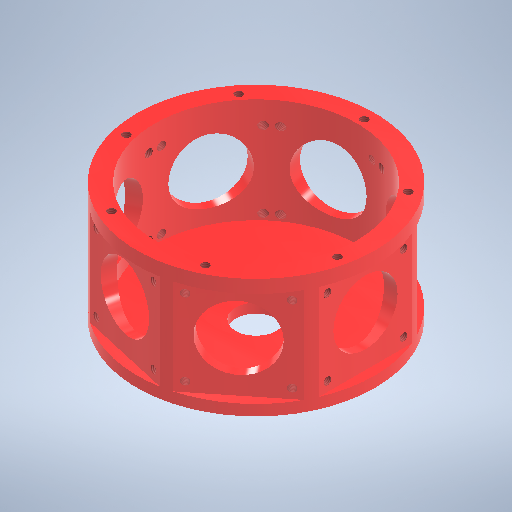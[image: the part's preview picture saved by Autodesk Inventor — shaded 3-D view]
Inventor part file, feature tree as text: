
AUTODESK INVENTOR PART (.ipt)
format: ipt  version: 2025 (Build 290162010, 162A)  size: 514,560 bytes
history: native  units: mm
features: sketch x11, extrude x6, hole x6, pattern_circular x5, plane x1
ambient origin geometry x8: Origin, YZ Plane, XZ Plane, XY Plane, X Axis, Y Axis, Z Axis, Center Point
bodies: Volumenkörper1 (feature_tree)
feature tree (29):
  extrude  "Extrusion1"  Depth=50.0mm TaperAngle=0.0deg
  plane  "Arbeitsebene1"
  extrude  "Extrusion2"  Depth=50.0mm
  pattern_circular  "Runde Anordnung1"  Count=4  [1 undecoded]
  sketch  "Skizze6"  dims[d7=4.0mm d8=0.0mm d9=70.0mm d10=360.0deg]
  extrude  "Extrusion9"  Depth=4.0mm TaperAngle=360.0deg
  extrude  "Extrusion10"  Depth=80.0mm
  extrude  "Extrusion11"  Depth=4.0mm TaperAngle=0.0deg
  hole  "Hole5"  [1 undecoded]
  hole  "Hole6"  [1 undecoded]
  hole  "Hole7"  [1 undecoded]
  hole  "Hole8"  [1 undecoded]
  pattern_circular  "Circular Pattern4"  Count=7 Angle=360.0deg
  extrude  "Extrusion12"  Depth=12.0mm
  pattern_circular  "Circular Pattern5"  [2 undecoded]
  hole  "Hole10"  [1 undecoded]
  pattern_circular  "Circular Pattern6"  [2 undecoded]
  hole  "Hole11"  [1 undecoded]
  pattern_circular  "Circular Pattern7"  [2 undecoded]
  sketch  "Skizze1"  dims[d0=100.0mm d1=50.0mm d2=0.0mm]
  sketch  "Skizze2"  dims[d3=50.0mm d5=40.0mm d6=40.0mm]
  sketch  "Sketch20"  dims[d25=85.0mm d26=80.0mm]
  sketch  "Sketch21"  dims[d76=4.5mm d78=4.0mm d79=0.0mm]
  sketch  "Sketch22"  dims[d80=4.0mm d81=0.0mm d85=43.0mm]
  sketch  "Sketch24"  dims[d87=4.0mm d88=0.0mm]
  sketch  "Sketch25"  dims[d89=17.1mm d90=6.0mm d91=4.0mm d92=2.0mm d93=90.0deg d94=4.0mm d95=0.0mm]
  sketch  "Sketch27"  dims[d96=85.0mm d97=6.0mm d98=4.0mm d99=2.0mm d100=90.0deg d101=44.0mm d102=0.0mm]
  sketch  "Sketch31"  dims[d104=35.0mm d105=6.0mm d106=4.0mm d107=2.0mm d108=90.0deg d109=11.0mm d110=0.0mm d111=32.0mm]
  sketch  "Sketch32"  dims[d112=32.0mm d113=16.0mm d114=16.0mm d115=3.242mm d116=8.0mm d117=4.0mm d118=2.0mm d119=90.0deg d120=10.0mm d121=20.594885mm d122=70.0mm d123=360.0deg d132=27.0mm d134=10.0mm d135=0.0mm d136=70.0mm d137=360.0deg d142=92.0mm d143=4.0mm d144=6.0mm d145=4.0mm d146=2.0mm d147=90.0deg d148=4.0mm d149=0.0mm d150=70.0mm d151=360.0deg d153=24.5mm d154=91.0mm d155=3.242mm d156=8.0mm d157=4.0mm d158=2.0mm d159=90.0deg d160=12.0mm d161=0.0mm d162=70.0mm d163=360.0deg]
note: 13 required parameter values undecoded (feature->parameter linkage not recoverable at this tier; creation-order binding heuristic only, values carry confidence <= 0.55)
